# Revit family: KOMFORT EC LB
name_source: partatom
category: Оборудование
units: mm (PartAtom-declared; Revit-internal decimal feet)

## family parameters
Всегда вертикально = Да
Классификация = Нет
На основе рабочей плоскости = Нет
Общий = Нет
При загрузке вырезать с полостями = Нет
Размер круглого соединителя = Использовать диаметр
Тип детали = Нормальный
Точка принадлежности помещению = Нет

## types (12) — shared parameters
00_20_Manufacturer = Blauberg
00_20_Name = Air handling unit
Casing Material = Steel, galvanized
Filter = G4/G4+F7
Frequency = 50 Гц
Load Classification = HVAC
Maintenance zone material = <По категории>
Number of Fase = 1
Temperature of moving air = -25…+40°С
URL = https://blaubergventilatoren.de
Voltage = 230 В
Изготовитель = Blauberg
zero-valued in all types: Отметка по умолчанию

## per-type parameters (varying)
| type | Amperage | B | B1 | B2 | D | Diameter | Dy | H | H1 | H2 | H3 | Height | L | L1 | Leg | Length | Maximum Air Flow | Power | Sound pressure level at 3 m distance | Weight | Width | direction | l1 |
| KOMFORT EC LB 300-E S21 | 1 А | 566 мм | 379 мм | 189 мм | 160 мм | 160 мм | 155 мм | 479 мм | 311 мм | 118 мм | 499 мм | 499 мм | 1083 мм | 1180 мм | 72 мм | 1180 мм | 380.0 м³/ч | 182 Вт | 24 dBA | 63.10 кг | 566 мм | 462 мм | 590 мм |
| KOMFORT EC LB 400 S21 | 2 А | 682 мм | 465 мм | 217 мм | 200 мм | 200 мм | 195 мм | 504 мм | 342 мм | 141 мм | 524 мм | 524 мм | 1094 мм | 1191 мм | 73 мм | 1191 мм | 540.0 м³/ч | 289 Вт | 27 dBA | 74.80 кг | 682 мм | 467 мм | 596 мм |
| KOMFORT EC LB 700-E S21 | 2 А | 866 мм | 570 мм | 296 мм | 250 мм | 250 мм | 245 мм | 601 мм | 400 мм | 166 мм | 621 мм | 621 мм | 1282 мм | 1379 мм | 85 мм | 1379 мм | 830.0 м³/ч | 336 Вт | 31 dBA | 107.00 кг | 866 мм | 561 мм | 690 мм |
| KOMFORT EC LBE 300-E S21 | 14 А | 566 мм | 379 мм | 189 мм | 160 мм | 160 мм | 155 мм | 479 мм | 311 мм | 118 мм | 499 мм | 499 мм | 1083 мм | 1180 мм | 72 мм | 1180 мм | 380.0 м³/ч | 2982 Вт | 24 dBA | 64.30 кг | 566 мм | 462 мм | 590 мм |
| KOMFORT EC LBE 400-E S21 | 14 А | 682 мм | 465 мм | 217 мм | 200 мм | 200 мм | 195 мм | 504 мм | 342 мм | 141 мм | 524 мм | 524 мм | 1094 мм | 1191 мм | 73 мм | 1191 мм | 540.0 м³/ч | 3089 Вт | 27 dBA | 76.00 кг | 682 мм | 467 мм | 596 мм |
| KOMFORT EC LBE 700-E S21 | 18 А | 866 мм | 570 мм | 296 мм | 250 мм | 250 мм | 245 мм | 601 мм | 400 мм | 166 мм | 621 мм | 621 мм | 1282 мм | 1379 мм | 85 мм | 1379 мм | 830.0 м³/ч | 3936 Вт | 31 dBA | 108.40 кг | 866 мм | 561 мм | 690 мм |
| KOMFORT EC LB 300 S21 | 1 А | 566 мм | 379 мм | 189 мм | 160 мм | 160 мм | 155 мм | 479 мм | 311 мм | 118 мм | 499 мм | 499 мм | 1083 мм | 1180 мм | 72 мм | 1180 мм | 380.0 м³/ч | 182 Вт | 24 dBA | 63.10 кг | 566 мм | 462 мм | 590 мм |
| KOMFORT EC LBE 300 S21 | 14 А | 566 мм | 379 мм | 189 мм | 160 мм | 160 мм | 155 мм | 479 мм | 311 мм | 118 мм | 499 мм | 499 мм | 1083 мм | 1180 мм | 72 мм | 1180 мм | 380.0 м³/ч | 2982 Вт | 24 dBA | 64.30 кг | 566 мм | 462 мм | 590 мм |
| KOMFORT EC LB 400-E S21 | 2 А | 682 мм | 465 мм | 217 мм | 200 мм | 200 мм | 195 мм | 504 мм | 342 мм | 141 мм | 524 мм | 524 мм | 1094 мм | 1191 мм | 73 мм | 1191 мм | 540.0 м³/ч | 289 Вт | 27 dBA | 74.80 кг | 682 мм | 467 мм | 596 мм |
| KOMFORT EC LBE 400 S21 | 14 А | 682 мм | 465 мм | 217 мм | 200 мм | 200 мм | 195 мм | 504 мм | 342 мм | 141 мм | 524 мм | 524 мм | 1094 мм | 1191 мм | 73 мм | 1191 мм | 540.0 м³/ч | 3089 Вт | 27 dBA | 76.00 кг | 682 мм | 467 мм | 596 мм |
| KOMFORT EC LB 700 S21 | 2 А | 866 мм | 570 мм | 296 мм | 250 мм | 250 мм | 245 мм | 601 мм | 400 мм | 166 мм | 621 мм | 621 мм | 1282 мм | 1379 мм | 85 мм | 1379 мм | 830.0 м³/ч | 336 Вт | 31 dBA | 107.00 кг | 866 мм | 561 мм | 690 мм |
| KOMFORT EC LBE 700 S21 | 18 А | 866 мм | 570 мм | 296 мм | 250 мм | 250 мм | 245 мм | 601 мм | 400 мм | 166 мм | 621 мм | 621 мм | 1282 мм | 1379 мм | 85 мм | 1379 мм | 830.0 м³/ч | 3936 Вт | 31 dBA | 108.40 кг | 866 мм | 561 мм | 690 мм |

note: column(s) folded — value = type name in every type: 00_20_Type
